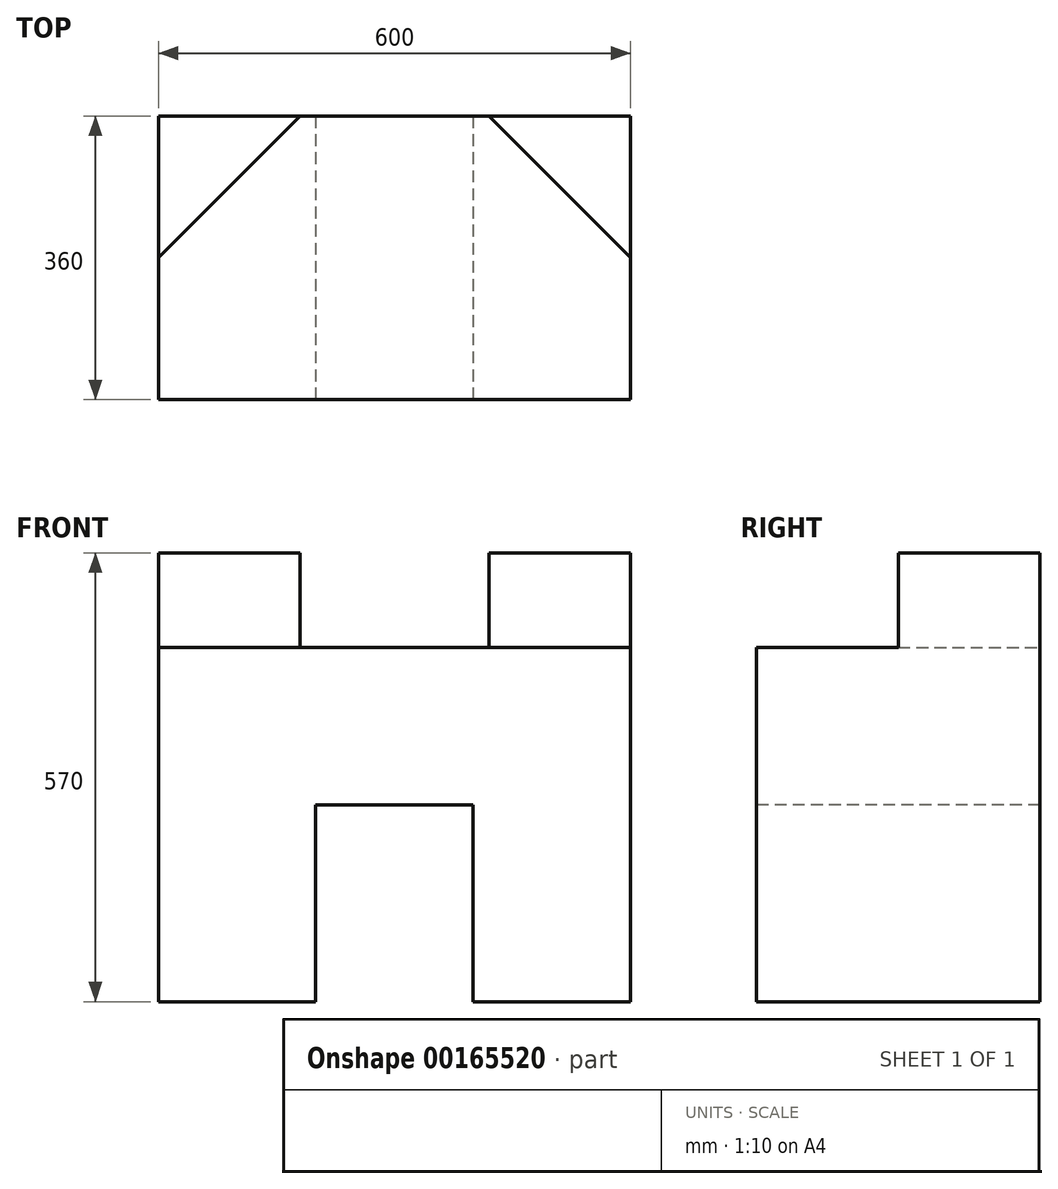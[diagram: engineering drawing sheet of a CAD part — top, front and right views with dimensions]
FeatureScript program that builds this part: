
annotation { "Feature Type Name" : "Feature", "Feature Type Description" : "" }
export const myFeature = defineFeature(function(context is Context, id is Id, definition is map)
    precondition{}
    {
        {
            var Q0;
            Q0=qCreatedBy(makeId("Front.planeOp"),FACE);
            var sketch = newSketch(context, id + "F0", { "sketchPlane" : qUnion([Q0])});
            skLineSegment(sketch, "E0.bottom", {"start": v(300, -285) * mm, "end": v(-300, -285) * mm});
            skLineSegment(sketch, "E0.top", {"start": v(300, 285) * mm, "end": v(-300, 285) * mm});
            skLineSegment(sketch, "E0.left", {"start": v(300, -285) * mm, "end": v(300, 285) * mm});
            skLineSegment(sketch, "E0.right", {"start": v(-300, -285) * mm, "end": v(-300, 285) * mm});
            skPoint(sketch, "E0.middle", {"position": v(0, 0) * mm});
            skSolve(sketch);
        }
        {
            var Q0;
            Q0 = qSketchRegion(id + "F0", true);
            extrude(context, id + "F1", {"entities" : qUnion([Q0]), "depth" : 360 * mm});
        }
        {
            var Q0;
            Q0=makeQuery(id+"F1.opExtrude","CAP_FACE",FACE,{"disambiguationData":[OSD([sQuery(id+"F0.wireOp",EDGE,"E0.bottom"),sQuery(id+"F0.wireOp",EDGE,"E0.top"),sQuery(id+"F0.wireOp",EDGE,"E0.left"),sQuery(id+"F0.wireOp",EDGE,"E0.right")])],"isStart":false});
            var sketch = newSketch(context, id + "F2", { "sketchPlane" : qUnion([Q0])});
            skLineSegment(sketch, "E1.bottom", {"start": v(100, -535) * mm, "end": v(-100, -535) * mm});
            skLineSegment(sketch, "E1.top", {"start": v(100, -35) * mm, "end": v(-100, -35) * mm});
            skLineSegment(sketch, "E1.left", {"start": v(100, -535) * mm, "end": v(100, -35) * mm});
            skLineSegment(sketch, "E1.right", {"start": v(-100, -535) * mm, "end": v(-100, -35) * mm});
            skPoint(sketch, "E1.middle", {"position": v(0, -285) * mm});
            skSolve(sketch);
        }
        {
            var Q0;
            Q0 = qSketchRegion(id + "F2", true);
            extrude(context, id + "F3", {"entities" : qUnion([Q0]), "operationType" : NewBodyOperationType.REMOVE, "endBound" : BoundingType.THROUGH_ALL, "oppositeDirection" : true, "depth" : 25 * mm});
        }
        {
            var Q0;
            Q0=makeQuery(id+"F1.opExtrude","SWEPT_FACE",FACE,{"disambiguationData":[OSD([sQuery(id+"F0.wireOp",EDGE,"E0.top")])]});
            var sketch = newSketch(context, id + "F4", { "sketchPlane" : qUnion([Q0])});
            skLineSegment(sketch, "E2", {"start": v(-300, -360) * mm, "end": v(-300, -180) * mm});
            skLineSegment(sketch, "E3", {"start": v(-300, -180) * mm, "end": v(-120, 0) * mm});
            skLineSegment(sketch, "E4", {"start": v(-120, 0) * mm, "end": v(120, 0) * mm});
            skLineSegment(sketch, "E5", {"start": v(120, 0) * mm, "end": v(300, -180) * mm});
            skLineSegment(sketch, "E6", {"start": v(300, -180) * mm, "end": v(300, -360) * mm});
            skLineSegment(sketch, "E7", {"start": v(300, -360) * mm, "end": v(-300, -360) * mm});
            skPoint(sketch, "E8", {"position": v(0, 0) * mm});
            skSolve(sketch);
        }
        {
            var Q0;
            Q0 = qSketchRegion(id + "F4", true);
            extrude(context, id + "F5", {"entities" : qUnion([Q0]), "operationType" : NewBodyOperationType.REMOVE, "oppositeDirection" : true, "depth" : 120 * mm});
        }
    });
